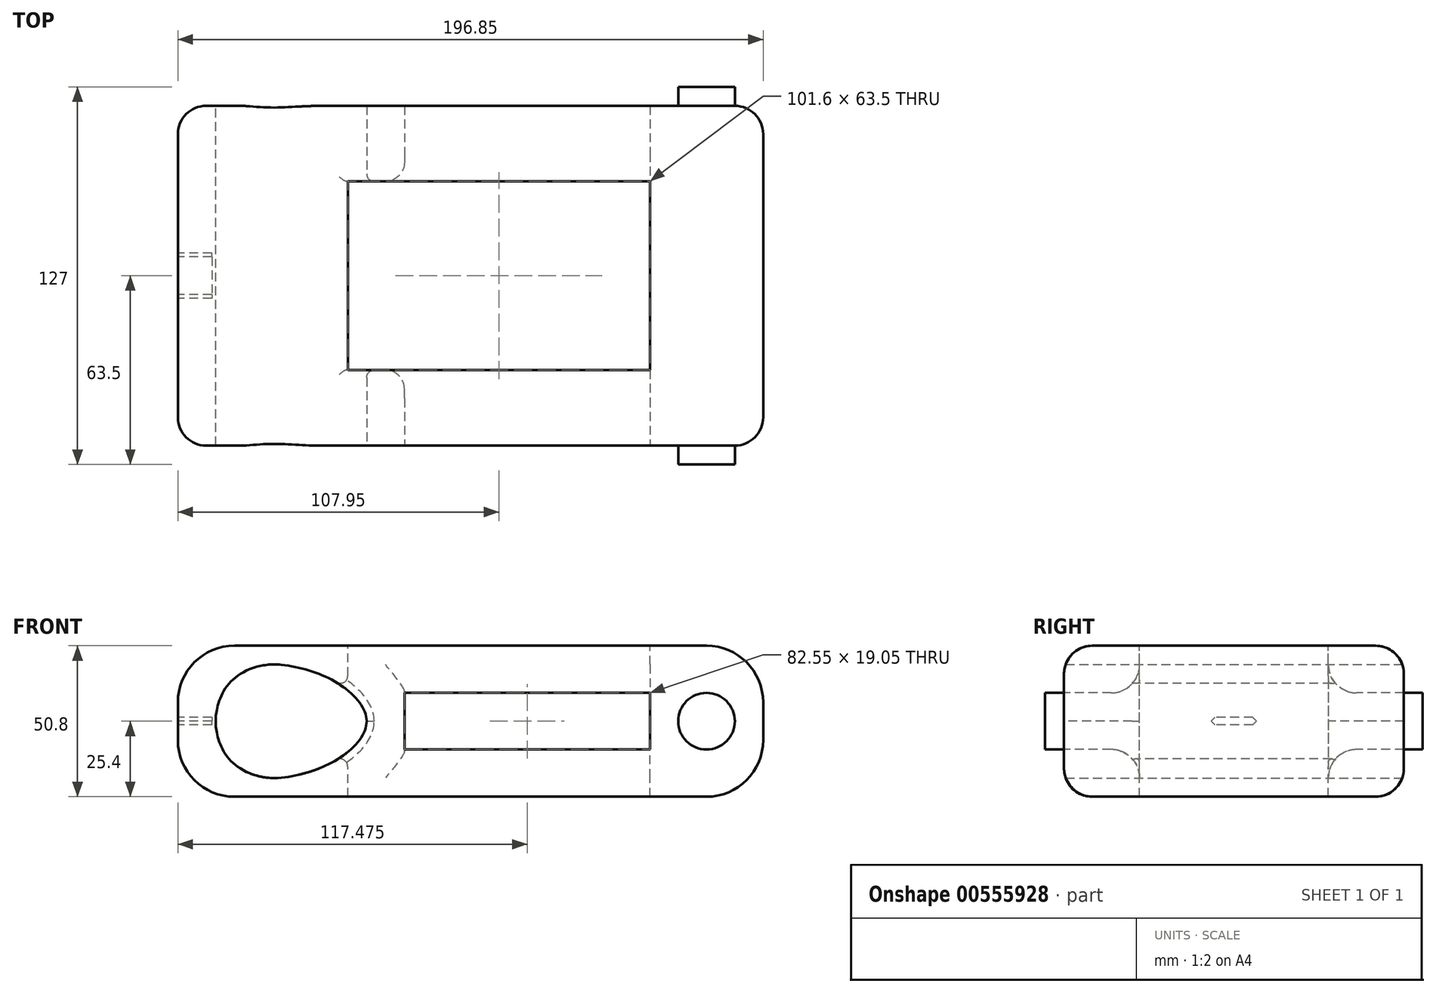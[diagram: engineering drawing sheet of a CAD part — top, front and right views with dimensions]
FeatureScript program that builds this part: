
annotation { "Feature Type Name" : "Feature", "Feature Type Description" : "" }
export const myFeature = defineFeature(function(context is Context, id is Id, definition is map)
    precondition{}
    {
        {
            var Q0;
            Q0=qCreatedBy(makeId("Front.planeOp"),FACE);
            var sketch = newSketch(context, id + "F0", { "sketchPlane" : qUnion([Q0])});
            skLineSegment(sketch, "E0.bottom", {"start": v(-196.85, 25.4) * mm, "end": v(0, 25.4) * mm});
            skLineSegment(sketch, "E0.top", {"start": v(-196.85, -25.4) * mm, "end": v(0, -25.4) * mm});
            skLineSegment(sketch, "E0.left", {"start": v(-196.85, 25.4) * mm, "end": v(-196.85, -25.4) * mm});
            skLineSegment(sketch, "E0.right", {"start": v(0, 25.4) * mm, "end": v(0, -25.4) * mm});
            skSolve(sketch);
        }
        {
            var Q0;
            Q0=makeQuery(id+"F0.imprint","IMPRINT",FACE,{"disambiguationData":[TD([[makeQuery(id+"F0.imprint","IMPRINT",EDGE,{"derivedFrom":sQuery(id+"F0.wireOp",EDGE,"E0.bottom")}),-1.0]])]});
            extrude(context, id + "F1", {"entities" : qUnion([Q0]), "depth" : 114.3 * mm, "offsetDistance" : 25.4 * mm, "symmetric" : true});
        }
        {
            var Q0;
            Q0=makeQuery(id+"F1.opExtrude","CAP_FACE",FACE,{"disambiguationData":[OSD([sQuery(id+"F0.wireOp",EDGE,"E0.bottom"),sQuery(id+"F0.wireOp",EDGE,"E0.top"),sQuery(id+"F0.wireOp",EDGE,"E0.left"),sQuery(id+"F0.wireOp",EDGE,"E0.right")])],"isStart":false});
            var sketch = newSketch(context, id + "F2", { "sketchPlane" : qUnion([Q0])});
            skLineSegment(sketch, "E1", {"start": v(0, 0) * mm, "end": v(-19.05, 0) * mm, "construction": true});
            skCircle(sketch, "E2", {"center": v(-19.05, 0) * mm, "radius": 9.53 * mm});
            skSolve(sketch);
        }
        {
            var Q0;
            Q0=makeQuery(id+"F2.imprint","IMPRINT",FACE,{"disambiguationData":[TD([[makeQuery(id+"F2.imprint","IMPRINT",EDGE,{"derivedFrom":sQuery(id+"F2.wireOp",EDGE,"E2")}),1.0]])]});
            extrude(context, id + "F3", {"entities" : qUnion([Q0]), "operationType" : NewBodyOperationType.ADD, "depth" : 6.35 * mm, "offsetDistance" : 25.4 * mm});
        }
        {
            var Q0;
            Q0=makeQuery(id+"F1.opExtrude","SWEPT_EDGE",EDGE,{"disambiguationData":[OSD([sQuery(id+"F0.wireOp",EDGE,"E0.bottom"),sQuery(id+"F0.wireOp",EDGE,"E0.right")])]});
            var Q1;
            Q1=makeQuery(id+"F1.opExtrude","SWEPT_EDGE",EDGE,{"disambiguationData":[OSD([sQuery(id+"F0.wireOp",EDGE,"E0.top"),sQuery(id+"F0.wireOp",EDGE,"E0.right")])]});
            fillet(context, id + "F4", {"entities" : qUnion([Q0, Q1]), "radius" : 19.05 * mm, "tangentPropagation" : true, "allowEdgeOverflow" : false});
        }
        {
            var Q0;
            Q0=makeQuery(id+"F1.opExtrude","SWEPT_EDGE",EDGE,{"disambiguationData":[OSD([sQuery(id+"F0.wireOp",EDGE,"E0.bottom"),sQuery(id+"F0.wireOp",EDGE,"E0.left")])]});
            var Q1;
            Q1=makeQuery(id+"F1.opExtrude","SWEPT_EDGE",EDGE,{"disambiguationData":[OSD([sQuery(id+"F0.wireOp",EDGE,"E0.top"),sQuery(id+"F0.wireOp",EDGE,"E0.left")])]});
            fillet(context, id + "F5", {"entities" : qUnion([Q0, Q1]), "radius" : 19.05 * mm, "tangentPropagation" : true, "allowEdgeOverflow" : false});
        }
        {
            var Q0;
            Q0=makeQuery(id+"F1.opExtrude","CAP_FACE",FACE,{"disambiguationData":[OSD([sQuery(id+"F0.wireOp",EDGE,"E0.bottom"),sQuery(id+"F0.wireOp",EDGE,"E0.top"),sQuery(id+"F0.wireOp",EDGE,"E0.left"),sQuery(id+"F0.wireOp",EDGE,"E0.right")])],"isStart":false});
            var sketch = newSketch(context, id + "F6", { "sketchPlane" : qUnion([Q0])});
            skLineSegment(sketch, "E3", {"start": v(0, 0) * mm, "end": v(-196.85, 0) * mm, "construction": true});
            skLineSegment(sketch, "E4", {"start": v(-196.85, 0) * mm, "end": v(-184.15, 0) * mm, "construction": true});
            skLineSegment(sketch, "E5", {"start": v(-184.15, 0) * mm, "end": v(-165.1, 0) * mm, "construction": true});
            skLineSegment(sketch, "E6", {"start": v(-165.1, 0) * mm, "end": v(-133.35, 0) * mm, "construction": true});
            skCircle(sketch, "E7", {"center": v(-165.1, 0) * mm, "radius": 19.05 * mm, "construction": true});
            skFitSpline(sketch, "E8", {"points": [v(-184.15, 0) * mm, v(-183.78, 3.75) * mm, v(-179.52, 12.82) * mm, v(-168.28, 18.78) * mm, v(-156.52, 18.07) * mm, v(-144.96, 13.86) * mm, v(-135.76, 6.37) * mm, v(-133.35, 0) * mm], "startDerivative": vector(-0.06, 31.12) * mm, "endDerivative": vector(0.61, -49.97) * mm});
            skFitSpline(sketch, "E9.MirrorCS", {"points": [v(-184.15, 0) * mm, v(-183.78, -3.75) * mm, v(-179.52, -12.82) * mm, v(-168.28, -18.78) * mm, v(-156.52, -18.07) * mm, v(-144.96, -13.86) * mm, v(-135.76, -6.37) * mm, v(-133.35, 0) * mm], "startDerivative": vector(-0.06, -31.12) * mm, "endDerivative": vector(0.61, 49.97) * mm});
            skLineSegment(sketch, "E10.bottom", {"start": v(-120.65, 9.53) * mm, "end": v(-38.1, 9.53) * mm});
            skLineSegment(sketch, "E10.top", {"start": v(-120.65, -9.52) * mm, "end": v(-38.1, -9.52) * mm});
            skLineSegment(sketch, "E10.left", {"start": v(-120.65, 9.53) * mm, "end": v(-120.65, -9.52) * mm});
            skLineSegment(sketch, "E10.right", {"start": v(-38.1, 9.53) * mm, "end": v(-38.1, -9.52) * mm});
            skSolve(sketch);
        }
        {
            var Q0;
            Q0=makeQuery(id+"F6.imprint","IMPRINT",FACE,{"disambiguationData":[TD([[makeQuery(id+"F6.imprint","IMPRINT",EDGE,{"derivedFrom":sQuery(id+"F6.wireOp",EDGE,"E8")}),-1.0]])]});
            var Q1;
            Q1=makeQuery(id+"F6.imprint","IMPRINT",FACE,{"disambiguationData":[TD([[makeQuery(id+"F6.imprint","IMPRINT",EDGE,{"derivedFrom":sQuery(id+"F6.wireOp",EDGE,"E10.bottom")}),-1.0]])]});
            var Q2;
            Q2=makeQuery(id+"F1.opExtrude","CAP_FACE",FACE,{"disambiguationData":[OSD([sQuery(id+"F0.wireOp",EDGE,"E0.bottom"),sQuery(id+"F0.wireOp",EDGE,"E0.top"),sQuery(id+"F0.wireOp",EDGE,"E0.left"),sQuery(id+"F0.wireOp",EDGE,"E0.right")])],"isStart":true});
            extrude(context, id + "F7", {"entities" : qUnion([Q0, Q1]), "operationType" : NewBodyOperationType.REMOVE, "endBound" : BoundingType.UP_TO_SURFACE, "oppositeDirection" : true, "depth" : 25.4 * mm, "endBoundEntityFace" : qUnion([Q2]), "offsetDistance" : 25.4 * mm});
        }
        {
            var Q0;
            Q0=makeQuery(id+"F1.opExtrude","SWEPT_FACE",FACE,{"disambiguationData":[OSD([sQuery(id+"F0.wireOp",EDGE,"E0.bottom")])]});
            var sketch = newSketch(context, id + "F8", { "sketchPlane" : qUnion([Q0])});
            skLineSegment(sketch, "E11.0.0", {"start": v(-19.05, 57.15) * mm, "end": v(-177.8, 57.15) * mm});
            skLineSegment(sketch, "E11.0.1", {"start": v(-177.8, 57.15) * mm, "end": v(-177.8, -57.15) * mm});
            skLineSegment(sketch, "E11.0.2", {"start": v(-177.8, -57.15) * mm, "end": v(-19.05, -57.15) * mm});
            skLineSegment(sketch, "E11.0.3", {"start": v(-19.05, -57.15) * mm, "end": v(-19.05, 57.15) * mm});
            skLineSegment(sketch, "E12.0", {"start": v(-44.45, 31.75) * mm, "end": v(-139.7, 31.75) * mm});
            skLineSegment(sketch, "E12.2", {"start": v(-139.7, -31.75) * mm, "end": v(-44.45, -31.75) * mm});
            skLineSegment(sketch, "E13", {"start": v(-139.7, 31.75) * mm, "end": v(-139.7, -31.75) * mm});
            skLineSegment(sketch, "E14", {"start": v(-44.45, 31.75) * mm, "end": v(-38.1, 31.75) * mm});
            skLineSegment(sketch, "E15", {"start": v(-38.1, 31.75) * mm, "end": v(-38.1, -31.75) * mm});
            skLineSegment(sketch, "E16", {"start": v(-44.45, -31.75) * mm, "end": v(-38.1, -31.75) * mm});
            skSolve(sketch);
        }
        {
            var Q0;
            Q0=makeQuery(id+"F8.imprint","IMPRINT",FACE,{"disambiguationData":[TD([[makeQuery(id+"F8.imprint","IMPRINT",EDGE,{"derivedFrom":sQuery(id+"F8.wireOp",EDGE,"E12.0")}),1.0]])]});
            var Q1;
            Q1=makeQuery(id+"F1.opExtrude","SWEPT_FACE",FACE,{"disambiguationData":[OSD([sQuery(id+"F0.wireOp",EDGE,"E0.top")])]});
            extrude(context, id + "F9", {"entities" : qUnion([Q0]), "operationType" : NewBodyOperationType.REMOVE, "endBound" : BoundingType.UP_TO_SURFACE, "oppositeDirection" : true, "depth" : 25.4 * mm, "endBoundEntityFace" : qUnion([Q1]), "offsetDistance" : 25.4 * mm});
        }
        {
            var Q0;
            Q0=makeQuery(id+"F7.boolean.opBoolean","COPY",EDGE,{"derivedFrom":makeQuery(id+"F7.opExtrude","CAP_EDGE",EDGE,{"disambiguationData":[OSD([sQuery(id+"F6.wireOp",EDGE,"E10.left")])],"isStart":true})});
            var Q1;
            Q1=makeQuery(id+"F7.boolean.opBoolean","COPY",EDGE,{"derivedFrom":makeQuery(id+"F7.opExtrude","CAP_EDGE",EDGE,{"disambiguationData":[OSD([sQuery(id+"F6.wireOp",EDGE,"E10.bottom")])],"isStart":true})});
            var Q2;
            Q2=makeQuery(id+"F7.boolean.opBoolean","COPY",EDGE,{"derivedFrom":makeQuery(id+"F7.opExtrude","CAP_EDGE",EDGE,{"disambiguationData":[OSD([sQuery(id+"F6.wireOp",EDGE,"E10.right")])],"isStart":true})});
            var Q3;
            Q3=makeQuery(id+"F7.boolean.opBoolean","COPY",EDGE,{"derivedFrom":makeQuery(id+"F7.opExtrude","CAP_EDGE",EDGE,{"disambiguationData":[OSD([sQuery(id+"F6.wireOp",EDGE,"E10.top")])],"isStart":true})});
            var Q4;
            Q4=makeQuery(id+"F7.boolean.opBoolean","COPY",EDGE,{"derivedFrom":makeQuery(id+"F7.opExtrude","CAP_EDGE",EDGE,{"disambiguationData":[OSD([sQuery(id+"F6.wireOp",EDGE,"E10.top")])],"isStart":false})});
            var Q5;
            Q5=makeQuery(id+"F7.boolean.opBoolean","COPY",EDGE,{"derivedFrom":makeQuery(id+"F7.opExtrude","CAP_EDGE",EDGE,{"disambiguationData":[OSD([sQuery(id+"F6.wireOp",EDGE,"E10.right")])],"isStart":false})});
            var Q6;
            Q6=makeQuery(id+"F7.boolean.opBoolean","COPY",EDGE,{"derivedFrom":makeQuery(id+"F7.opExtrude","CAP_EDGE",EDGE,{"disambiguationData":[OSD([sQuery(id+"F6.wireOp",EDGE,"E10.left")])],"isStart":false})});
            var Q7;
            Q7=makeQuery(id+"F9.boolean.opBoolean","COPY",EDGE,{"derivedFrom":makeQuery(id+"F9.opExtrude","CAP_EDGE",EDGE,{"disambiguationData":[OSD([sQuery(id+"F8.wireOp",EDGE,"E12.2"),sQuery(id+"F8.wireOp",EDGE,"E16")])],"isStart":true})});
            var Q8;
            Q8=makeQuery(id+"F9.boolean.opBoolean","COPY",EDGE,{"derivedFrom":makeQuery(id+"F9.opExtrude","CAP_EDGE",EDGE,{"disambiguationData":[OSD([sQuery(id+"F8.wireOp",EDGE,"E12.0"),sQuery(id+"F8.wireOp",EDGE,"E14")])],"isStart":true})});
            var Q9;
            Q9=makeQuery(id+"F9.boolean.opBoolean","COPY",EDGE,{"derivedFrom":makeQuery(id+"F9.opExtrude","CAP_EDGE",EDGE,{"disambiguationData":[OSD([sQuery(id+"F8.wireOp",EDGE,"E13")])],"isStart":true})});
            var Q10;
            Q10=makeQuery(id+"F9.boolean.opBoolean","COPY",EDGE,{"derivedFrom":makeQuery(id+"F9.opExtrude","CAP_EDGE",EDGE,{"disambiguationData":[OSD([sQuery(id+"F8.wireOp",EDGE,"E15")])],"isStart":true})});
            var Q11;
            Q11=makeQuery(id+"F9.boolean.opBoolean","COPY",EDGE,{"derivedFrom":makeQuery(id+"F9.opExtrude","CAP_EDGE",EDGE,{"disambiguationData":[OSD([sQuery(id+"F8.wireOp",EDGE,"E13")])],"isStart":false})});
            var Q12;
            Q12=makeQuery(id+"F9.boolean.opBoolean","COPY",EDGE,{"derivedFrom":makeQuery(id+"F9.opExtrude","CAP_EDGE",EDGE,{"disambiguationData":[OSD([sQuery(id+"F8.wireOp",EDGE,"E12.0"),sQuery(id+"F8.wireOp",EDGE,"E14")])],"isStart":false})});
            var Q13;
            Q13=makeQuery(id+"F9.boolean.opBoolean","COPY",EDGE,{"derivedFrom":makeQuery(id+"F9.opExtrude","CAP_EDGE",EDGE,{"disambiguationData":[OSD([sQuery(id+"F8.wireOp",EDGE,"E15")])],"isStart":false})});
            var Q14;
            Q14=makeQuery(id+"F9.boolean.opBoolean","COPY",EDGE,{"derivedFrom":makeQuery(id+"F9.opExtrude","CAP_EDGE",EDGE,{"disambiguationData":[OSD([sQuery(id+"F8.wireOp",EDGE,"E12.2"),sQuery(id+"F8.wireOp",EDGE,"E16")])],"isStart":false})});
            var Q15;
            Q15=makeQuery(id+"F9.boolean.opBoolean","INTERSECT",EDGE,{"derivedFrom":[makeQuery(id+"F7.boolean.opBoolean","COPY",FACE,{"derivedFrom":makeQuery(id+"F7.opExtrude","SWEPT_FACE",FACE,{"disambiguationData":[OSD([sQuery(id+"F6.wireOp",EDGE,"E10.left")])]})}),makeQuery(id+"F9.opExtrude","SWEPT_FACE",FACE,{"disambiguationData":[OSD([sQuery(id+"F8.wireOp",EDGE,"E12.0"),sQuery(id+"F8.wireOp",EDGE,"E14")])]})]});
            var Q16;
            Q16=makeQuery(id+"F9.boolean.opBoolean","INTERSECT",EDGE,{"derivedFrom":[makeQuery(id+"F7.boolean.opBoolean","COPY",FACE,{"derivedFrom":makeQuery(id+"F7.opExtrude","SWEPT_FACE",FACE,{"disambiguationData":[OSD([sQuery(id+"F6.wireOp",EDGE,"E10.left")])]})}),makeQuery(id+"F9.opExtrude","SWEPT_FACE",FACE,{"disambiguationData":[OSD([sQuery(id+"F8.wireOp",EDGE,"E12.2"),sQuery(id+"F8.wireOp",EDGE,"E16")])]})]});
            var Q17;
            Q17=makeQuery(id+"F7.boolean.opBoolean","COPY",EDGE,{"derivedFrom":makeQuery(id+"F7.opExtrude","CAP_EDGE",EDGE,{"disambiguationData":[OSD([sQuery(id+"F6.wireOp",EDGE,"E10.bottom")])],"isStart":false})});
            fillet(context, id + "F10", {"entities" : qUnion([Q0, Q1, Q2, Q3, Q4, Q5, Q6, Q7, Q8, Q9, Q10, Q11, Q12, Q13, Q14, Q15, Q16, Q17]), "radius" : 6.35 * mm, "tangentPropagation" : true, "allowEdgeOverflow" : false});
        }
        {
            var Q0;
            Q0=makeQuery(id+"F9.boolean.opBoolean","INTERSECT",EDGE,{"derivedFrom":[makeQuery(id+"F7.boolean.opBoolean","COPY",FACE,{"derivedFrom":makeQuery(id+"F7.opExtrude","SWEPT_FACE",FACE,{"disambiguationData":[OSD([sQuery(id+"F6.wireOp",EDGE,"E10.top")])]})}),makeQuery(id+"F9.opExtrude","SWEPT_FACE",FACE,{"disambiguationData":[OSD([sQuery(id+"F8.wireOp",EDGE,"E12.0"),sQuery(id+"F8.wireOp",EDGE,"E14")])]})]});
            var Q1;
            Q1=makeQuery(id+"F9.boolean.opBoolean","INTERSECT",EDGE,{"derivedFrom":[makeQuery(id+"F7.boolean.opBoolean","COPY",FACE,{"derivedFrom":makeQuery(id+"F7.opExtrude","SWEPT_FACE",FACE,{"disambiguationData":[OSD([sQuery(id+"F6.wireOp",EDGE,"E10.bottom")])]})}),makeQuery(id+"F9.opExtrude","SWEPT_FACE",FACE,{"disambiguationData":[OSD([sQuery(id+"F8.wireOp",EDGE,"E12.0"),sQuery(id+"F8.wireOp",EDGE,"E14")])]})]});
            var Q2;
            Q2=makeQuery(id+"F9.boolean.opBoolean","INTERSECT",EDGE,{"derivedFrom":[makeQuery(id+"F7.boolean.opBoolean","COPY",FACE,{"derivedFrom":makeQuery(id+"F7.opExtrude","SWEPT_FACE",FACE,{"disambiguationData":[OSD([sQuery(id+"F6.wireOp",EDGE,"E10.bottom")])]})}),makeQuery(id+"F9.opExtrude","SWEPT_FACE",FACE,{"disambiguationData":[OSD([sQuery(id+"F8.wireOp",EDGE,"E12.2"),sQuery(id+"F8.wireOp",EDGE,"E16")])]})]});
            var Q3;
            Q3=makeQuery(id+"F9.boolean.opBoolean","INTERSECT",EDGE,{"derivedFrom":[makeQuery(id+"F7.boolean.opBoolean","COPY",FACE,{"derivedFrom":makeQuery(id+"F7.opExtrude","SWEPT_FACE",FACE,{"disambiguationData":[OSD([sQuery(id+"F6.wireOp",EDGE,"E10.top")])]})}),makeQuery(id+"F9.opExtrude","SWEPT_FACE",FACE,{"disambiguationData":[OSD([sQuery(id+"F8.wireOp",EDGE,"E12.2"),sQuery(id+"F8.wireOp",EDGE,"E16")])]})]});
            var Q4;
            Q4=makeQuery(id+"F1.opExtrude","CAP_EDGE",EDGE,{"disambiguationData":[OSD([sQuery(id+"F0.wireOp",EDGE,"E0.bottom")])],"isStart":false});
            var Q5;
            Q5=makeQuery(id+"F1.opExtrude","CAP_EDGE",EDGE,{"disambiguationData":[OSD([sQuery(id+"F0.wireOp",EDGE,"E0.bottom")])],"isStart":true});
            fillet(context, id + "F11", {"entities" : qUnion([Q0, Q1, Q2, Q3, Q4, Q5]), "radius" : 9.52 * mm, "tangentPropagation" : true, "allowEdgeOverflow" : false});
        }
        {
            var Q0;
            Q0=makeQuery(id+"F1.opExtrude","SWEPT_FACE",FACE,{"disambiguationData":[OSD([sQuery(id+"F0.wireOp",EDGE,"E0.left")])]});
            var sketch = newSketch(context, id + "F12", { "sketchPlane" : qUnion([Q0])});
            skLineSegment(sketch, "E17.bottom", {"start": v(-6.35, 1.27) * mm, "end": v(6.35, 1.27) * mm});
            skLineSegment(sketch, "E17.top", {"start": v(-6.35, -1.27) * mm, "end": v(6.35, -1.27) * mm});
            skLineSegment(sketch, "E17.left", {"start": v(-6.35, 1.27) * mm, "end": v(-6.35, -1.27) * mm});
            skLineSegment(sketch, "E17.right", {"start": v(6.35, 1.27) * mm, "end": v(6.35, -1.27) * mm});
            skLineSegment(sketch, "E18", {"start": v(6.35, 0) * mm, "end": v(7.62, 0) * mm, "construction": true});
            skPoint(sketch, "E18.endSnap0", {"position": v(6.35, 0) * mm});
            skLineSegment(sketch, "E19", {"start": v(-6.35, 0) * mm, "end": v(-7.62, 0) * mm, "construction": true});
            skPoint(sketch, "E19.endSnap0", {"position": v(-6.35, 0) * mm});
            skLineSegment(sketch, "E20", {"start": v(-6.35, -1.27) * mm, "end": v(-7.62, 0) * mm});
            skLineSegment(sketch, "E21", {"start": v(-6.35, 1.27) * mm, "end": v(-7.62, 0) * mm});
            skLineSegment(sketch, "E22", {"start": v(6.35, 1.27) * mm, "end": v(7.62, 0) * mm});
            skLineSegment(sketch, "E23", {"start": v(6.35, -1.27) * mm, "end": v(7.62, 0) * mm});
            skSolve(sketch);
        }
        {
            var Q0;
            Q0=makeQuery(id+"F12.imprint","IMPRINT",FACE,{"disambiguationData":[TD([[makeQuery(id+"F12.imprint","IMPRINT",EDGE,{"derivedFrom":sQuery(id+"F12.wireOp",EDGE,"E17.bottom")}),-1.0]])]});
            var Q1;
            Q1=makeQuery(id+"F12.imprint","IMPRINT",FACE,{"disambiguationData":[TD([[makeQuery(id+"F12.imprint","IMPRINT",EDGE,{"derivedFrom":sQuery(id+"F12.wireOp",EDGE,"E17.right")}),1.0]])]});
            var Q2;
            Q2=makeQuery(id+"F12.imprint","IMPRINT",FACE,{"disambiguationData":[TD([[makeQuery(id+"F12.imprint","IMPRINT",EDGE,{"derivedFrom":sQuery(id+"F12.wireOp",EDGE,"E17.left")}),-1.0]])]});
            extrude(context, id + "F13", {"entities" : qUnion([Q0, Q1, Q2]), "operationType" : NewBodyOperationType.REMOVE, "oppositeDirection" : true, "depth" : 11.43 * mm, "offsetDistance" : 25.4 * mm});
        }
        {
            var Q0;
            Q0=makeQuery(id+"F11.opFillet","SPLIT",FACE,{"disambiguationData":[OD(0.0)],"derivedFrom":makeQuery(id+"F1.opExtrude","CAP_FACE",FACE,{"disambiguationData":[OSD([sQuery(id+"F0.wireOp",EDGE,"E0.bottom"),sQuery(id+"F0.wireOp",EDGE,"E0.top"),sQuery(id+"F0.wireOp",EDGE,"E0.left"),sQuery(id+"F0.wireOp",EDGE,"E0.right")])],"isStart":true})});
            var sketch = newSketch(context, id + "F14", { "sketchPlane" : qUnion([Q0])});
            skLineSegment(sketch, "E24", {"start": v(0, 0) * mm, "end": v(19.05, 0) * mm, "construction": true});
            skCircle(sketch, "E25", {"center": v(19.05, 0) * mm, "radius": 9.53 * mm});
            skSolve(sketch);
        }
        {
            var Q0;
            Q0=makeQuery(id+"F14.imprint","IMPRINT",FACE,{"disambiguationData":[TD([[makeQuery(id+"F14.imprint","IMPRINT",EDGE,{"derivedFrom":sQuery(id+"F14.wireOp",EDGE,"E25")}),1.0]])]});
            extrude(context, id + "F15", {"entities" : qUnion([Q0]), "operationType" : NewBodyOperationType.ADD, "depth" : 6.35 * mm, "offsetDistance" : 25.4 * mm});
        }
        {
            var Q0;
            Q0=makeQuery(id+"F9.boolean.opBoolean","INTERSECT",EDGE,{"derivedFrom":[makeQuery(id+"F7.boolean.opBoolean","COPY",FACE,{"derivedFrom":makeQuery(id+"F7.opExtrude","SWEPT_FACE",FACE,{"disambiguationData":[OSD([sQuery(id+"F6.wireOp",EDGE,"E9.MirrorCS")])]})}),makeQuery(id+"F9.opExtrude","SWEPT_FACE",FACE,{"disambiguationData":[OSD([sQuery(id+"F8.wireOp",EDGE,"E13")])]})]});
            var Q1;
            Q1=makeQuery(id+"F9.boolean.opBoolean","INTERSECT",EDGE,{"derivedFrom":[makeQuery(id+"F7.boolean.opBoolean","COPY",FACE,{"derivedFrom":makeQuery(id+"F7.opExtrude","SWEPT_FACE",FACE,{"disambiguationData":[OSD([sQuery(id+"F6.wireOp",EDGE,"E8")])]})}),makeQuery(id+"F9.opExtrude","SWEPT_FACE",FACE,{"disambiguationData":[OSD([sQuery(id+"F8.wireOp",EDGE,"E13")])]})]});
            var Q2;
            Q2=makeQuery(id+"F9.boolean.opBoolean","INTERSECT",EDGE,{"derivedFrom":[makeQuery(id+"F7.boolean.opBoolean","COPY",FACE,{"derivedFrom":makeQuery(id+"F7.opExtrude","SWEPT_FACE",FACE,{"disambiguationData":[OSD([sQuery(id+"F6.wireOp",EDGE,"E8")])]})}),makeQuery(id+"F9.opExtrude","SWEPT_FACE",FACE,{"disambiguationData":[OSD([sQuery(id+"F8.wireOp",EDGE,"E12.2"),sQuery(id+"F8.wireOp",EDGE,"E16")])]})]});
            var Q3;
            Q3=makeQuery(id+"F9.boolean.opBoolean","INTERSECT",EDGE,{"derivedFrom":[makeQuery(id+"F7.boolean.opBoolean","COPY",FACE,{"derivedFrom":makeQuery(id+"F7.opExtrude","SWEPT_FACE",FACE,{"disambiguationData":[OSD([sQuery(id+"F6.wireOp",EDGE,"E9.MirrorCS")])]})}),makeQuery(id+"F9.opExtrude","SWEPT_FACE",FACE,{"disambiguationData":[OSD([sQuery(id+"F8.wireOp",EDGE,"E12.2"),sQuery(id+"F8.wireOp",EDGE,"E16")])]})]});
            var Q4;
            Q4=makeQuery(id+"F9.boolean.opBoolean","INTERSECT",EDGE,{"derivedFrom":[makeQuery(id+"F7.boolean.opBoolean","COPY",FACE,{"derivedFrom":makeQuery(id+"F7.opExtrude","SWEPT_FACE",FACE,{"disambiguationData":[OSD([sQuery(id+"F6.wireOp",EDGE,"E9.MirrorCS")])]})}),makeQuery(id+"F9.opExtrude","SWEPT_FACE",FACE,{"disambiguationData":[OSD([sQuery(id+"F8.wireOp",EDGE,"E12.0"),sQuery(id+"F8.wireOp",EDGE,"E14")])]})]});
            var Q5;
            Q5=makeQuery(id+"F9.boolean.opBoolean","INTERSECT",EDGE,{"derivedFrom":[makeQuery(id+"F7.boolean.opBoolean","COPY",FACE,{"derivedFrom":makeQuery(id+"F7.opExtrude","SWEPT_FACE",FACE,{"disambiguationData":[OSD([sQuery(id+"F6.wireOp",EDGE,"E8")])]})}),makeQuery(id+"F9.opExtrude","SWEPT_FACE",FACE,{"disambiguationData":[OSD([sQuery(id+"F8.wireOp",EDGE,"E12.0"),sQuery(id+"F8.wireOp",EDGE,"E14")])]})]});
            fillet(context, id + "F16", {"entities" : qUnion([Q0, Q1, Q2, Q3, Q4, Q5]), "radius" : 2.54 * mm, "tangentPropagation" : true, "allowEdgeOverflow" : false});
        }
    });
